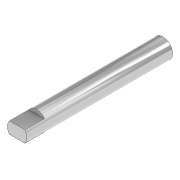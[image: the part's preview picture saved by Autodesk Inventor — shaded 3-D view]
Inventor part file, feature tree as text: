
AUTODESK INVENTOR PART (.ipt)
format: ipt  version: 2020 (Build 240168000, 168)  size: 91,136 bytes
history: native  units: in
note: dims shown in document units (in); Inventor stores cm internally (conversion verified against a paired STEP export)
features: extrude x2, sketch x2, projected_geometry x1
ambient origin geometry x8: Origin, YZ Plane, XZ Plane, XY Plane, X Axis, Y Axis, Z Axis, Center Point
bodies: Solid1 (feature_tree)
feature tree (5):
  extrude  "Extrusion1"  Depth=1.4764in TaperAngle=0.0deg
  extrude  "Extrusion2"  Depth=0.1969in
  sketch  "Sketch1"  dims[d0=0.1969in d1=1.4764in d2=0.0in]
  sketch  "Sketch2"  dims[d3=0.1181in d4=0.0591in d5=0.1969in d6=0.0in]
  projected_geometry  "Projected Loop1"
